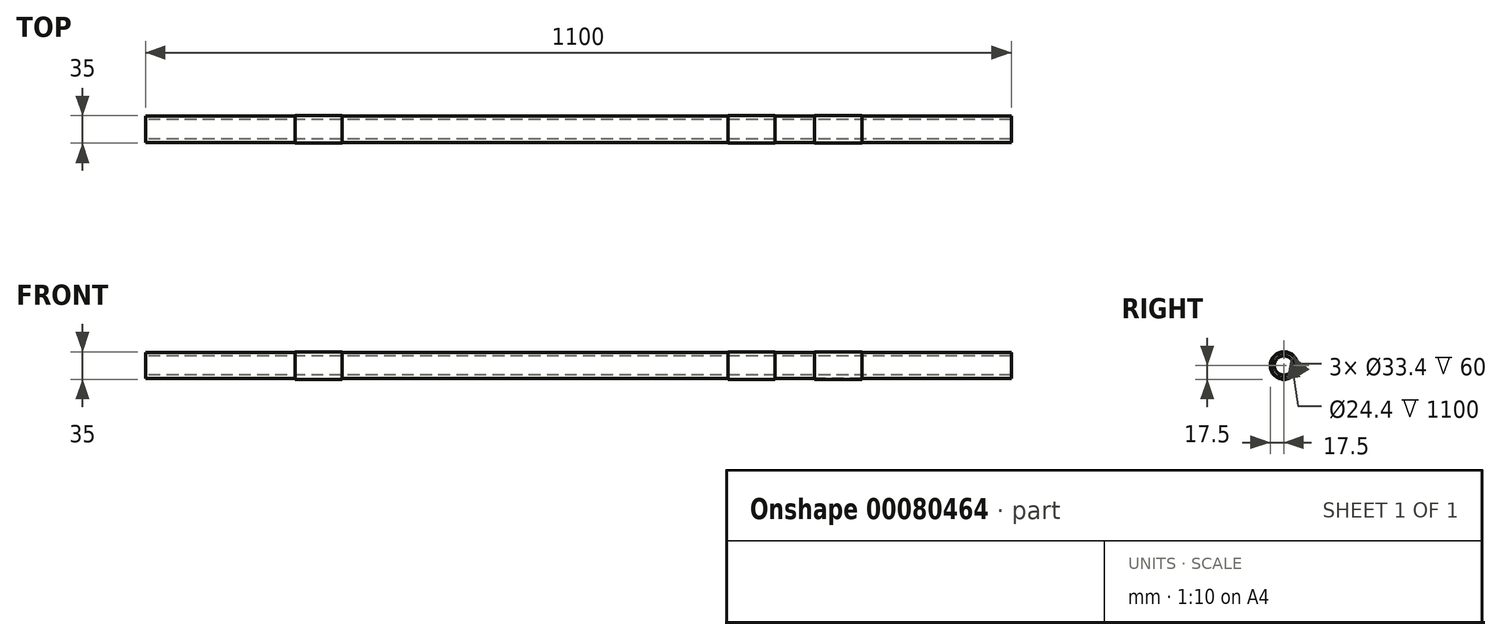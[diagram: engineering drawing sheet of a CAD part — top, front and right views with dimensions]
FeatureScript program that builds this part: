
annotation { "Feature Type Name" : "Feature", "Feature Type Description" : "" }
export const myFeature = defineFeature(function(context is Context, id is Id, definition is map)
    precondition{}
    {
        {
            var Q0;
            Q0=qCreatedBy(makeId("Right.planeOp"),FACE);
            var sketch = newSketch(context, id + "F0", { "sketchPlane" : qUnion([Q0])});
            skCircle(sketch, "E0", {"center": v(0, 0) * mm, "radius": 16.7 * mm});
            skCircle(sketch, "E1", {"center": v(0, 0) * mm, "radius": 12.2 * mm});
            skSolve(sketch);
        }
        {
            var Q0;
            Q0 = qSketchRegion(id + "F0", true);
            extrude(context, id + "F1", {"entities" : qUnion([Q0]), "depth" : 1100 * mm, "symmetric" : true});
        }
        {
            var Q0;
            Q0=qCreatedBy(makeId("Right.planeOp"),FACE);
            var sketch = newSketch(context, id + "F2", { "sketchPlane" : qUnion([Q0])});
            skCircle(sketch, "E2.0", {"center": v(0, 0) * mm, "radius": 16.7 * mm});
            skCircle(sketch, "E3", {"center": v(0, 0) * mm, "radius": 17.5 * mm});
            skSolve(sketch);
        }
        {
            var Q0;
            Q0 = qSketchRegion(id + "F2", true);
            extrude(context, id + "F3", {"entities" : qUnion([Q0]), "depth" : 60 * mm, "symmetric" : true});
        }
        {
            var Q0;
            Q0=makeQuery(id+"F3.opExtrude","SWEPT_BODY",BODY,{"disambiguationData":[OSD([sQuery(id+"F2.wireOp",EDGE,"E2.0"),sQuery(id+"F2.wireOp",EDGE,"E3")])]});
            transform(context, id + "F4", {"entities" : qUnion([Q0]), "transformType" : TransformType.TRANSLATION_3D, "dx" : 330 * mm, "dy" : 0 * mm, "dz" : 0 * mm, "makeCopy" : false});
        }
        {
            var Q0;
            Q0=makeQuery(id+"F3.opExtrude","SWEPT_BODY",BODY,{"disambiguationData":[OSD([sQuery(id+"F2.wireOp",EDGE,"E2.0"),sQuery(id+"F2.wireOp",EDGE,"E3")])]});
            var Q1;
            Q1=qCreatedBy(makeId("Right.planeOp"),FACE);
            mirror(context, id + "F5", {"entities" : qUnion([Q0]), "mirrorPlane" : qUnion([Q1])});
        }
        {
            var Q0;
            Q0=makeQuery(id+"F5.opPattern","COPY",BODY,{"derivedFrom":makeQuery(id+"F3.opExtrude","SWEPT_BODY",BODY,{"disambiguationData":[OSD([sQuery(id+"F2.wireOp",EDGE,"E2.0"),sQuery(id+"F2.wireOp",EDGE,"E3")])]}),"instanceName":"1"});
            transform(context, id + "F6", {"entities" : qUnion([Q0]), "transformType" : TransformType.TRANSLATION_3D, "dx" : 550 * mm, "dy" : 0 * mm, "dz" : 0 * mm, "makeCopy" : true});
        }
    });
